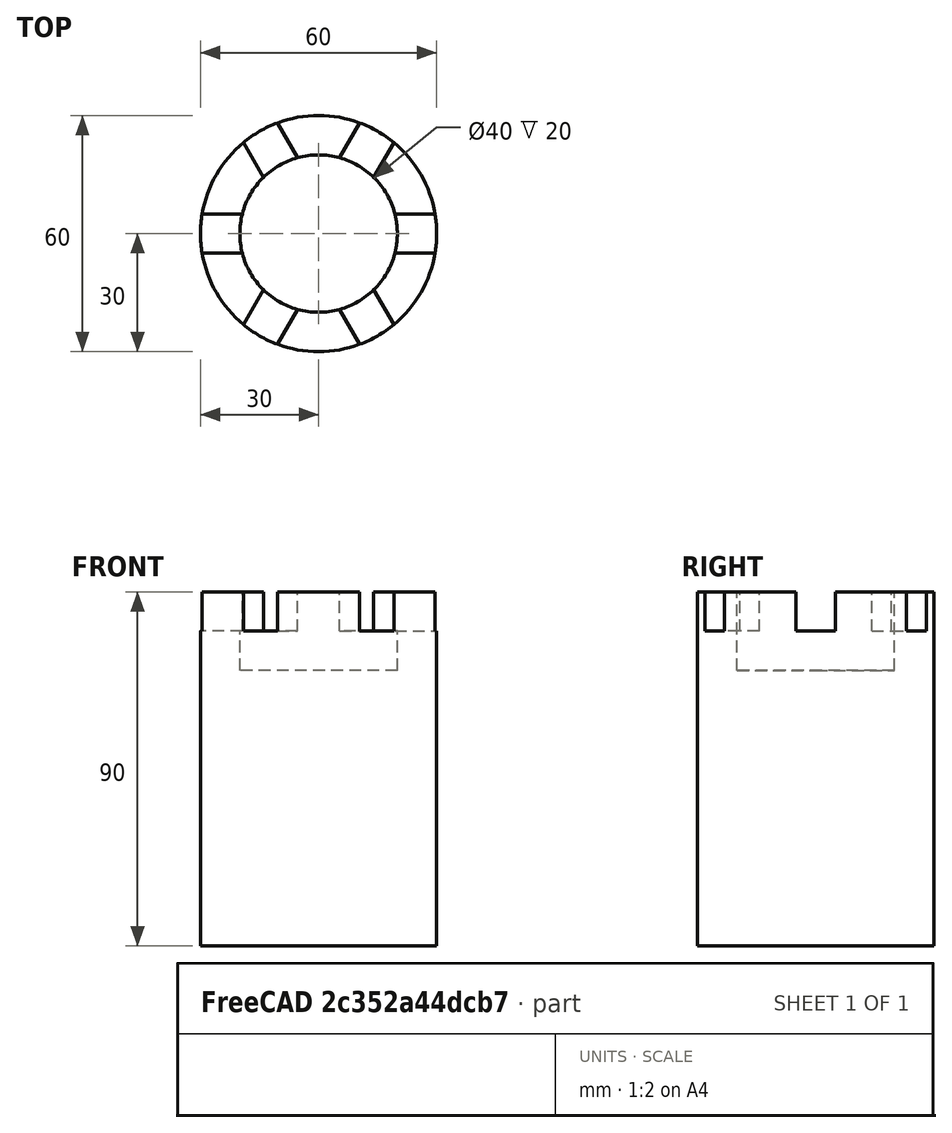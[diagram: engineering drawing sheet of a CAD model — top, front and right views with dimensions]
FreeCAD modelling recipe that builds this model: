
FCSTD DOCUMENT  (FreeCAD 0.16R6707 (Git))
Label: Torre
License: CreativeCommons Attribution-ShareAlike
LicenseURL: http://creativecommons.org/licenses/by-sa/4.0/
objects: Part::Cylinder×2, Part::Cut×2, Part::Box×1, Part::FeaturePython×1
note: 6 computed .brp shape members not serialized (recipe doc carries the construction recipe); baked Part::Feature solids carry a one-line shape summary decoded from their .brp

FEATURE [Part::Cylinder] Cylinder  label="Torrre"
  Angle = 360
  Height = 90
  Radius = 30
FEATURE [Part::Box] Box  label="Almena"
  Height = 10
  Length = 20
  Placement = pos=(15,-5,80) rot=(0,0,1;0rad)
  Width = 10
FEATURE [Part::Cylinder] Cylinder001  label="VaciadoTorre"
  Angle = 360
  Height = 20
  Placement = pos=(0,0,70) rot=(0,0,1;0rad)
  Radius = 20
FEATURE [Part::Cut] Cut  label="Vaciado_patio"
  Base = -> Cylinder
  Tool = -> Cylinder001
FEATURE [Part::FeaturePython] Array  label="Array_almenas"  # Draft array (typed FeaturePython)
  Angle = 360
  ArrayType = 1
  Axis = (0,0,1)
  Base = -> Box
  Center = (0,0,0)
  Fuse = false
  IntervalAxis = (0,0,0)
  IntervalX = (1,0,0)
  IntervalY = (0,1,0)
  IntervalZ = (0,0,0)
  NumberPolar = 6
  NumberX = 2
  NumberY = 2
  NumberZ = 1
FEATURE [Part::Cut] Cut001  label="Torre_acabada"
  Base = -> Cut
  Tool = -> Array
